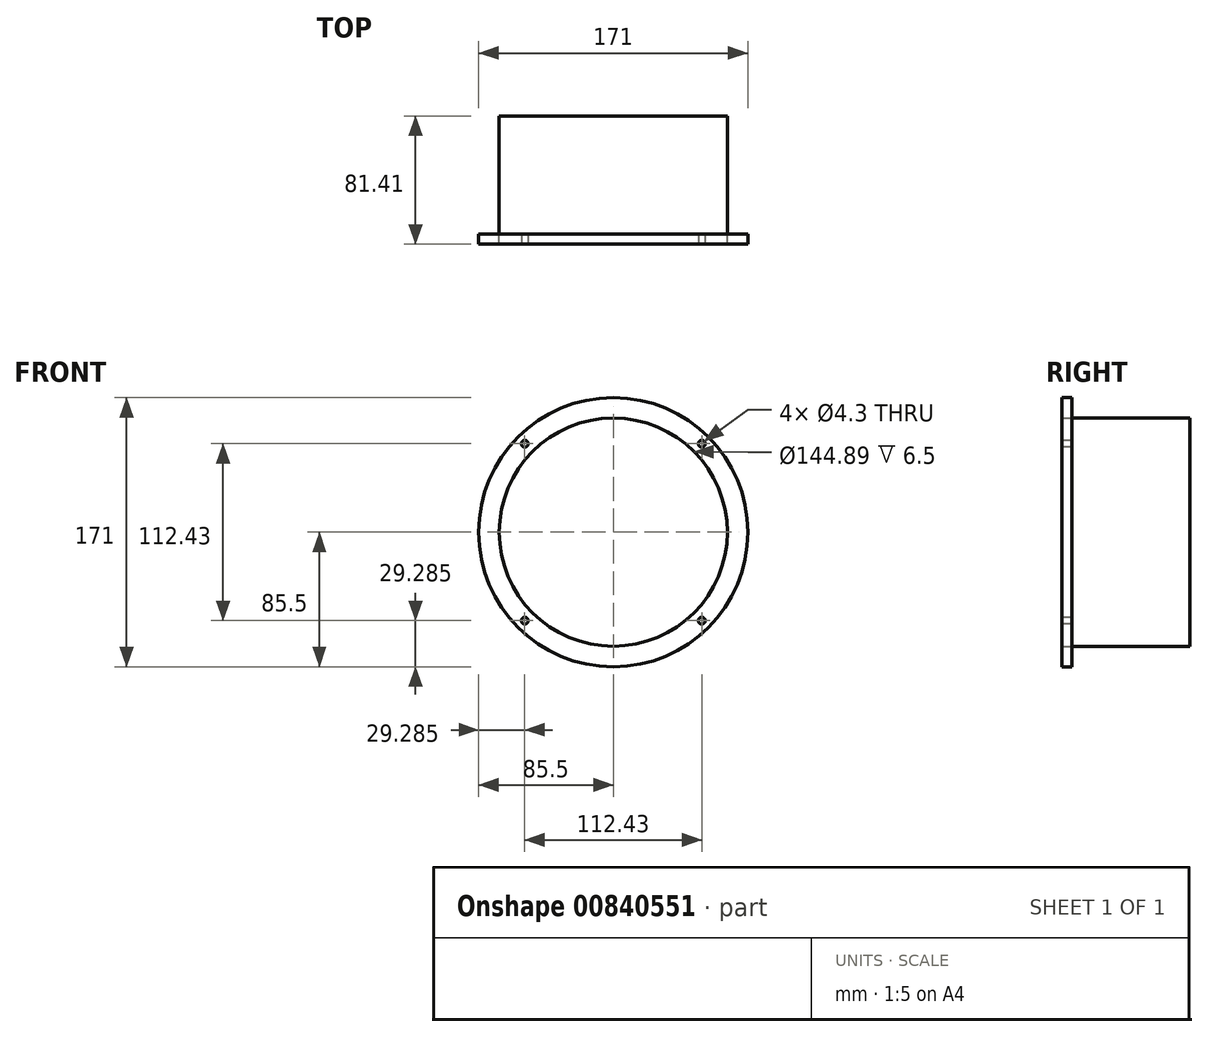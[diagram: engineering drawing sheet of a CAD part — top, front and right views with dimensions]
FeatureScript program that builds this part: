
annotation { "Feature Type Name" : "Feature", "Feature Type Description" : "" }
export const myFeature = defineFeature(function(context is Context, id is Id, definition is map)
    precondition{}
    {
        {
            var Q0;
            Q0=qCreatedBy(makeId("Front.planeOp"),FACE);
            var sketch = newSketch(context, id + "F0", { "sketchPlane" : qUnion([Q0])});
            skCircle(sketch, "E0", {"center": v(0, 0) * mm, "radius": 85.5 * mm});
            skCircle(sketch, "E1", {"center": v(0, 0) * mm, "radius": 79.5 * mm});
            skCircle(sketch, "E2", {"center": v(0, 0) * mm, "radius": 72.44 * mm});
            skSolve(sketch);
        }
        {
            var Q0;
            Q0=makeQuery(id+"F0.imprint","IMPRINT",FACE,{"disambiguationData":[TD([[makeQuery(id+"F0.imprint","IMPRINT",EDGE,{"derivedFrom":sQuery(id+"F0.wireOp",EDGE,"E0")}),1.0]])]});
            var Q1;
            Q1=makeQuery(id+"F0.imprint","IMPRINT",FACE,{"disambiguationData":[TD([[makeQuery(id+"F0.imprint","IMPRINT",EDGE,{"derivedFrom":sQuery(id+"F0.wireOp",EDGE,"E1")}),1.0]])]});
            extrude(context, id + "F1", {"entities" : qUnion([Q0, Q1]), "depth" : 6.5 * mm, "offsetDistance" : 25 * mm});
        }
        {
            var Q0;
            Q0=makeQuery(id+"F1.opExtrude","CAP_FACE",FACE,{"disambiguationData":[OSD([sQuery(id+"F0.wireOp",EDGE,"E0")])],"isStart":false});
            var sketch = newSketch(context, id + "F2", { "sketchPlane" : qUnion([Q0])});
            skLineSegment(sketch, "E3", {"start": v(0, 0) * mm, "end": v(-56.21, 56.21) * mm, "construction": true});
            skCircle(sketch, "E4", {"center": v(-56.21, 56.21) * mm, "radius": 4.25 * mm});
            skCircle(sketch, "E5", {"center": v(-56.21, 56.21) * mm, "radius": 2.15 * mm});
            skLineSegment(sketch, "E6", {"start": v(0, 0) * mm, "end": v(56.21, 56.21) * mm, "construction": true});
            skLineSegment(sketch, "E7", {"start": v(0, 0) * mm, "end": v(56.21, -56.21) * mm, "construction": true});
            skLineSegment(sketch, "E8", {"start": v(0, 0) * mm, "end": v(-56.21, -56.21) * mm, "construction": true});
            skCircle(sketch, "E9", {"center": v(56.21, 56.21) * mm, "radius": 4.25 * mm});
            skCircle(sketch, "E10", {"center": v(56.21, 56.21) * mm, "radius": 2.15 * mm});
            skCircle(sketch, "E11", {"center": v(56.21, -56.21) * mm, "radius": 4.25 * mm});
            skCircle(sketch, "E12", {"center": v(56.21, -56.21) * mm, "radius": 2.15 * mm});
            skCircle(sketch, "E13", {"center": v(-56.21, -56.21) * mm, "radius": 4.25 * mm});
            skCircle(sketch, "E14", {"center": v(-56.21, -56.21) * mm, "radius": 2.15 * mm});
            skSolve(sketch);
        }
        {
            var Q0;
            Q0=makeQuery(id+"F0.imprint","IMPRINT",FACE,{"disambiguationData":[TD([[makeQuery(id+"F0.imprint","IMPRINT",EDGE,{"derivedFrom":sQuery(id+"F0.wireOp",EDGE,"E2")}),1.0]])]});
            extrude(context, id + "F3", {"entities" : qUnion([Q0]), "depth" : -74.9 * mm, "offsetDistance" : 25 * mm});
        }
        {
            var Q0;
            Q0=sQuery(id+"F2.wireOp",VERTEX,"E3.end");
            var Q1;
            Q1=makeQuery(id+"F1.opExtrude","SWEPT_BODY",BODY,{"disambiguationData":[OSD([sQuery(id+"F0.wireOp",EDGE,"E0"),sQuery(id+"F0.wireOp",EDGE,"E2")])]});
            hole(context, id + "F4", {"style" : HoleStyle.SIMPLE, "endStyle" : HoleEndStyle.BLIND, "holeDiameter" : 4.3 * mm, "majorDiameter" : 5 * mm, "holeDepth" : 6.5 * mm, "isTappedThrough" : true, "tappedDepth" : 12 * mm, "tapClearance" : 3, "locations" : qUnion([Q0]), "scope" : qUnion([Q1])});
        }
        {
            var Q0;
            Q0=sQuery(id+"F2.wireOp",VERTEX,"E6.end");
            var Q1;
            Q1=makeQuery(id+"F1.opExtrude","SWEPT_BODY",BODY,{"disambiguationData":[OSD([sQuery(id+"F0.wireOp",EDGE,"E0"),sQuery(id+"F0.wireOp",EDGE,"E2")])]});
            hole(context, id + "F5", {"style" : HoleStyle.SIMPLE, "endStyle" : HoleEndStyle.BLIND, "holeDiameter" : 4.3 * mm, "majorDiameter" : 5 * mm, "holeDepth" : 6.5 * mm, "isTappedThrough" : true, "tappedDepth" : 12 * mm, "tapClearance" : 3, "locations" : qUnion([Q0]), "scope" : qUnion([Q1])});
        }
        {
            var Q0;
            Q0=sQuery(id+"F2.wireOp",VERTEX,"E7.end");
            var Q1;
            Q1=makeQuery(id+"F1.opExtrude","SWEPT_BODY",BODY,{"disambiguationData":[OSD([sQuery(id+"F0.wireOp",EDGE,"E0"),sQuery(id+"F0.wireOp",EDGE,"E2")])]});
            hole(context, id + "F6", {"style" : HoleStyle.SIMPLE, "endStyle" : HoleEndStyle.BLIND, "holeDiameter" : 4.3 * mm, "majorDiameter" : 5 * mm, "holeDepth" : 6.5 * mm, "isTappedThrough" : true, "tappedDepth" : 12 * mm, "tapClearance" : 3, "locations" : qUnion([Q0]), "scope" : qUnion([Q1])});
        }
        {
            var Q0;
            Q0=sQuery(id+"F2.wireOp",VERTEX,"E8.end");
            var Q1;
            Q1=makeQuery(id+"F1.opExtrude","SWEPT_BODY",BODY,{"disambiguationData":[OSD([sQuery(id+"F0.wireOp",EDGE,"E0"),sQuery(id+"F0.wireOp",EDGE,"E2")])]});
            hole(context, id + "F7", {"style" : HoleStyle.SIMPLE, "endStyle" : HoleEndStyle.BLIND, "holeDiameter" : 4.3 * mm, "majorDiameter" : 5 * mm, "holeDepth" : 6.5 * mm, "isTappedThrough" : true, "tappedDepth" : 12 * mm, "tapClearance" : 3, "locations" : qUnion([Q0]), "scope" : qUnion([Q1])});
        }
    });
